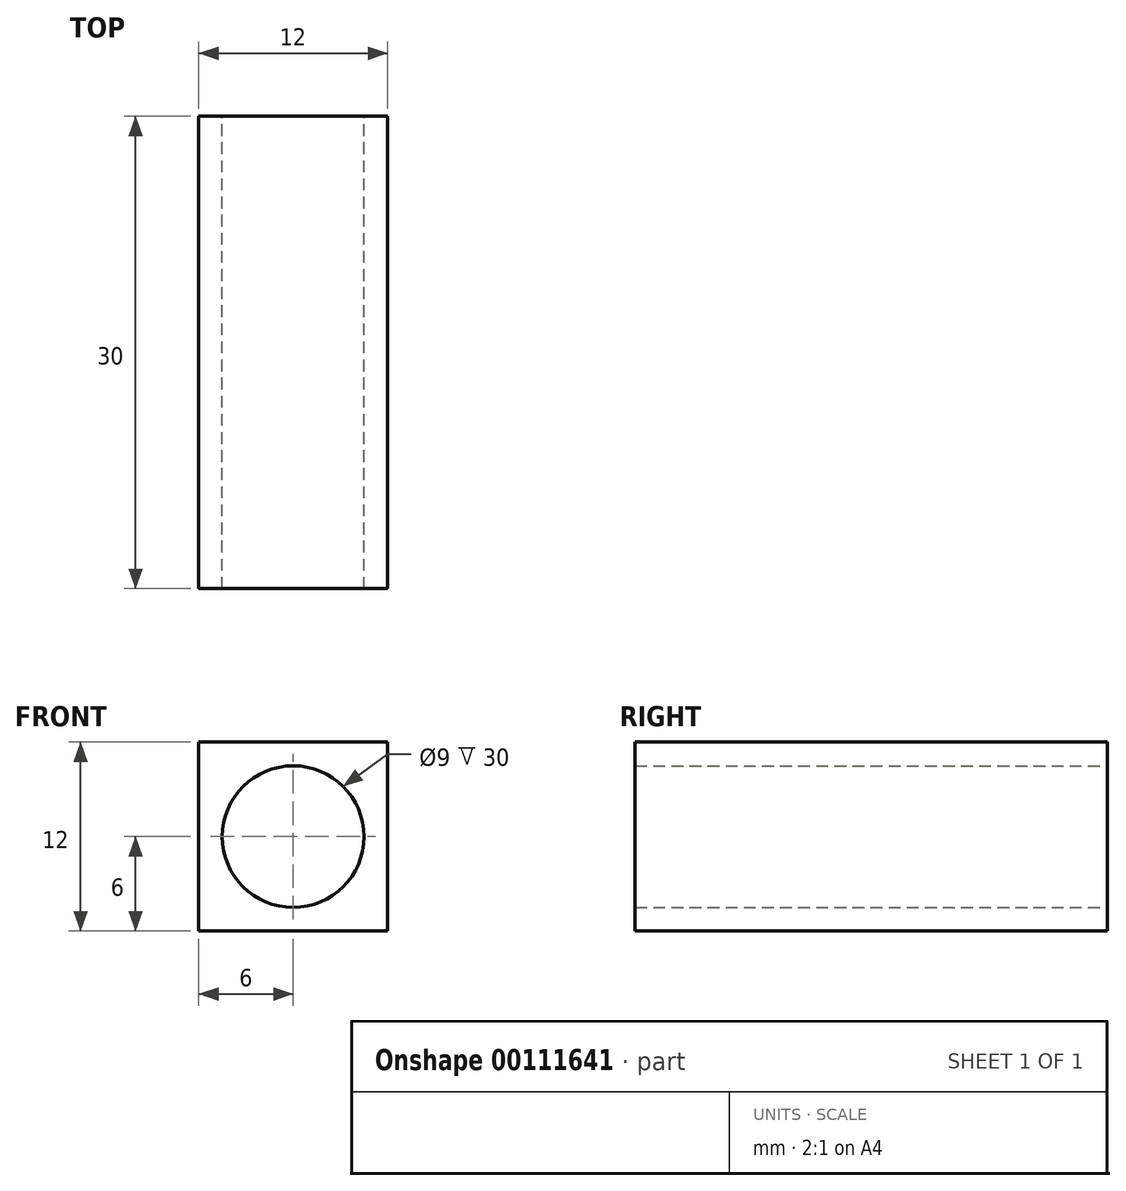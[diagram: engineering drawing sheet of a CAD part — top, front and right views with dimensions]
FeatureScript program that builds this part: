
annotation { "Feature Type Name" : "Feature", "Feature Type Description" : "" }
export const myFeature = defineFeature(function(context is Context, id is Id, definition is map)
    precondition{}
    {
        {
            var Q0;
            Q0=qCreatedBy(makeId("Front.planeOp"),FACE);
            var sketch = newSketch(context, id + "F0", { "sketchPlane" : qUnion([Q0])});
            skLineSegment(sketch, "E0.bottom", {"start": v(6, -6) * mm, "end": v(-6, -6) * mm});
            skLineSegment(sketch, "E0.top", {"start": v(6, 6) * mm, "end": v(-6, 6) * mm});
            skLineSegment(sketch, "E0.left", {"start": v(6, -6) * mm, "end": v(6, 6) * mm});
            skLineSegment(sketch, "E0.right", {"start": v(-6, -6) * mm, "end": v(-6, 6) * mm});
            skPoint(sketch, "E0.middle", {"position": v(0, 0) * mm});
            skCircle(sketch, "E1", {"center": v(0, 0) * mm, "radius": 4.5 * mm});
            skSolve(sketch);
        }
        {
            var Q0;
            Q0=qSketchRegion(id+"F0",true);
            extrude(context, id + "F1", {"entities" : qUnion([Q0]), "depth" : 30 * mm});
        }
    });
